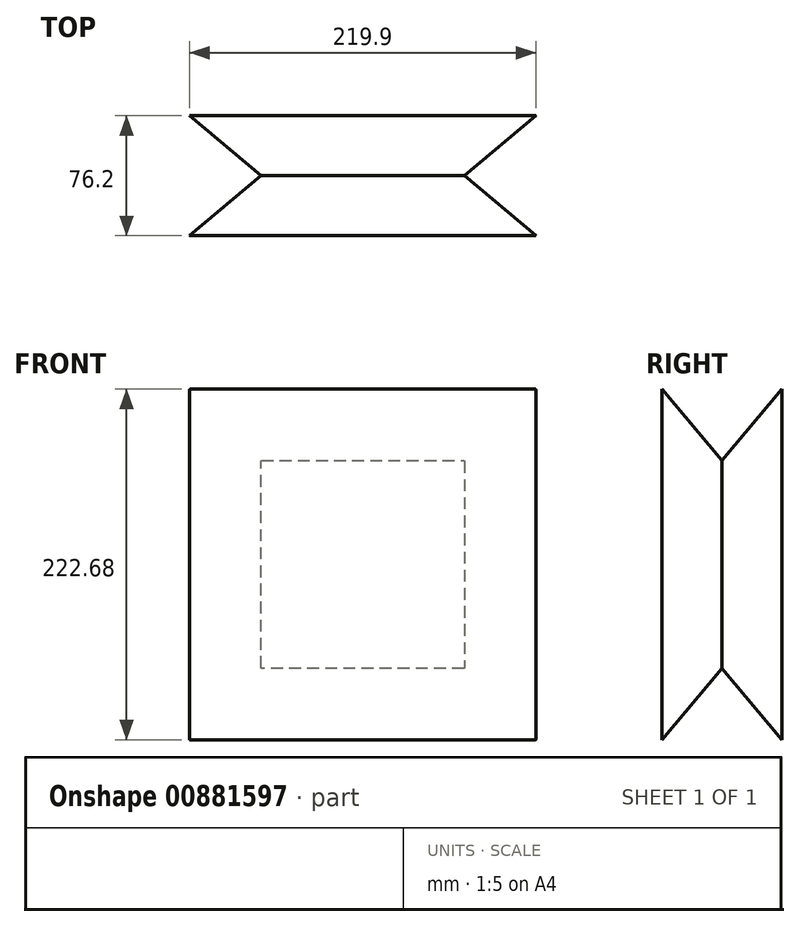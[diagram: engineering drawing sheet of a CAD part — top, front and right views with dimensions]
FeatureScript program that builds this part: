
annotation { "Feature Type Name" : "Feature", "Feature Type Description" : "" }
export const myFeature = defineFeature(function(context is Context, id is Id, definition is map)
    precondition{}
    {
        {
            var Q0;
            Q0=qCreatedBy(makeId("Front.planeOp"),FACE);
            var sketch = newSketch(context, id + "F0", { "sketchPlane" : qUnion([Q0])});
            skLineSegment(sketch, "E0.bottom", {"start": v(-64.54, -65.94) * mm, "end": v(64.54, -65.94) * mm});
            skLineSegment(sketch, "E0.top", {"start": v(-64.54, 65.94) * mm, "end": v(64.54, 65.94) * mm});
            skLineSegment(sketch, "E0.left", {"start": v(-64.54, -65.94) * mm, "end": v(-64.54, 65.94) * mm});
            skLineSegment(sketch, "E0.right", {"start": v(64.54, -65.94) * mm, "end": v(64.54, 65.94) * mm});
            skPoint(sketch, "E0.middle", {"position": v(0, 0) * mm});
            skSolve(sketch);
        }
        {
            var Q0;
            Q0 = qSketchRegion(id + "F0", true);
            extrude(context, id + "F1", {"entities" : qUnion([Q0]), "endBound" : BoundingType.SYMMETRIC, "depth" : 76.2 * mm, "offsetDistance" : 25.4 * mm, "hasDraft" : true, "draftAngle" : 50 * degree});
        }
        {
            var Q0;
            Q0=makeQuery(id+"F1.*.split.splitOp","SPLIT",EDGE,{"derivedFrom":makeQuery(id+"F1.opExtrude","SWEPT_EDGE",EDGE,{"disambiguationData":[OSD([sQuery(id+"F0.wireOp",EDGE,"E0.top"),sQuery(id+"F0.wireOp",EDGE,"E0.right")])]})});
            var Q1;
            Q1=makeQuery(id+"F1.*.split.splitOp","SPLIT",EDGE,{"derivedFrom":makeQuery(id+"F1.opExtrude","SWEPT_EDGE",EDGE,{"disambiguationData":[OSD([sQuery(id+"F0.wireOp",EDGE,"E0.top"),sQuery(id+"F0.wireOp",EDGE,"E0.left")])]})});
            var Q2;
            Q2=makeQuery(id+"F1.*.split.splitOp","SPLIT",EDGE,{"derivedFrom":makeQuery(id+"F1.opExtrude","SWEPT_EDGE",EDGE,{"disambiguationData":[OSD([sQuery(id+"F0.wireOp",EDGE,"E0.bottom"),sQuery(id+"F0.wireOp",EDGE,"E0.left")])]})});
            var Q3;
            Q3=makeQuery(id+"F1.*.split.splitOp","SPLIT",EDGE,{"derivedFrom":makeQuery(id+"F1.opExtrude","SWEPT_EDGE",EDGE,{"disambiguationData":[OSD([sQuery(id+"F0.wireOp",EDGE,"E0.bottom"),sQuery(id+"F0.wireOp",EDGE,"E0.right")])]})});
            var Q4;
            Q4=makeQuery(id+"F1.*.split.splitOp","SPLIT",EDGE,{"derivedFrom":makeQuery(id+"F1.opExtrude","SWEPT_EDGE",EDGE,{"disambiguationData":[OSD([sQuery(id+"F0.wireOp",EDGE,"E0.bottom"),sQuery(id+"F0.wireOp",EDGE,"E0.right")])]}),"isFromBackBody":true});
            var Q5;
            Q5=makeQuery(id+"F1.*.split.splitOp","SPLIT",EDGE,{"derivedFrom":makeQuery(id+"F1.opExtrude","SWEPT_EDGE",EDGE,{"disambiguationData":[OSD([sQuery(id+"F0.wireOp",EDGE,"E0.bottom"),sQuery(id+"F0.wireOp",EDGE,"E0.left")])]}),"isFromBackBody":true});
            var Q6;
            Q6=makeQuery(id+"F1.*.split.splitOp","SPLIT",EDGE,{"derivedFrom":makeQuery(id+"F1.opExtrude","SWEPT_EDGE",EDGE,{"disambiguationData":[OSD([sQuery(id+"F0.wireOp",EDGE,"E0.top"),sQuery(id+"F0.wireOp",EDGE,"E0.left")])]}),"isFromBackBody":true});
            var Q7;
            Q7=makeQuery(id+"F1.*.split.splitOp","SPLIT",EDGE,{"derivedFrom":makeQuery(id+"F1.opExtrude","SWEPT_EDGE",EDGE,{"disambiguationData":[OSD([sQuery(id+"F0.wireOp",EDGE,"E0.top"),sQuery(id+"F0.wireOp",EDGE,"E0.right")])]}),"isFromBackBody":true});
            fillet(context, id + "F2", {"entities" : qUnion([Q0, Q1, Q2, Q3, Q4, Q5, Q6, Q7]), "radius" : 0.5 * mm, "tangentPropagation" : true, "allowEdgeOverflow" : false});
        }
    });
